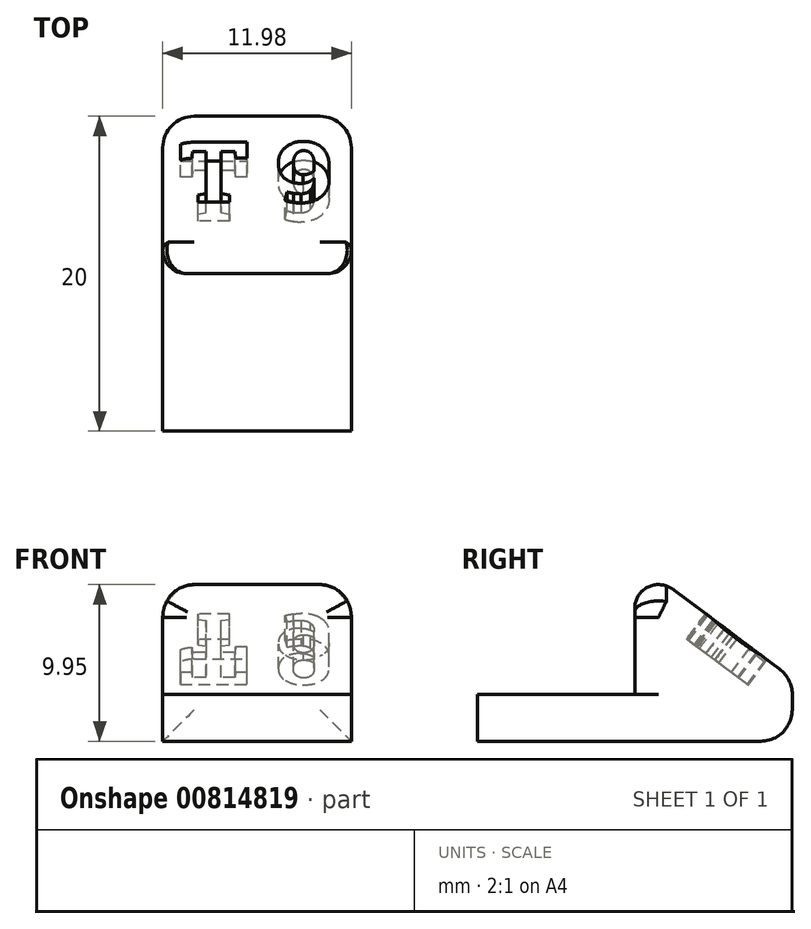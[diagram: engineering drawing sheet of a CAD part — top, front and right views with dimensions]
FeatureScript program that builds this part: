
annotation { "Feature Type Name" : "Feature", "Feature Type Description" : "" }
export const myFeature = defineFeature(function(context is Context, id is Id, definition is map)
    precondition{}
    {
        {
            var Q0;
            Q0=qCreatedBy(makeId("Top.planeOp"),FACE);
            var sketch = newSketch(context, id + "F0", { "sketchPlane" : qUnion([Q0])});
            skLineSegment(sketch, "E0.bottom", {"start": v(6, 10) * mm, "end": v(-5.99, 10) * mm});
            skLineSegment(sketch, "E0.top", {"start": v(6, -10) * mm, "end": v(-5.99, -10) * mm});
            skLineSegment(sketch, "E0.left", {"start": v(6, 10) * mm, "end": v(6, -10) * mm});
            skLineSegment(sketch, "E0.right", {"start": v(-5.99, 10) * mm, "end": v(-5.99, -10) * mm});
            skPoint(sketch, "E0.middle", {"position": v(0, 0) * mm});
            skSolve(sketch);
        }
        {
            var Q0;
            Q0=qSketchRegion(id+"F0",true);
            extrude(context, id + "F1", {"entities" : qUnion([Q0]), "depth" : 2.98 * mm, "offsetDistance" : 25 * mm});
        }
        {
            var Q0;
            Q0=makeQuery(id+"F1.opExtrude","CAP_FACE",FACE,{"disambiguationData":[OSD([sQuery(id+"F0.wireOp",EDGE,"E0.bottom"),sQuery(id+"F0.wireOp",EDGE,"E0.top"),sQuery(id+"F0.wireOp",EDGE,"E0.left"),sQuery(id+"F0.wireOp",EDGE,"E0.right")])],"isStart":false});
            var sketch = newSketch(context, id + "F2", { "sketchPlane" : qUnion([Q0])});
            skLineSegment(sketch, "E1.bottom", {"start": v(-5.99, 10) * mm, "end": v(6, 10) * mm});
            skLineSegment(sketch, "E1.top", {"start": v(-5.99, 0) * mm, "end": v(6, 0) * mm});
            skLineSegment(sketch, "E1.left", {"start": v(-5.99, 10) * mm, "end": v(-5.99, 0) * mm});
            skLineSegment(sketch, "E1.right", {"start": v(6, 10) * mm, "end": v(6, 0) * mm});
            skSolve(sketch);
        }
        {
            var Q0;
            Q0=makeQuery(id+"F2.imprint","IMPRINT",FACE,{"disambiguationData":[TD([[makeQuery(id+"F2.imprint","IMPRINT",EDGE,{"derivedFrom":sQuery(id+"F2.wireOp",EDGE,"E1.bottom")}),1.0]])]});
            extrude(context, id + "F3", {"entities" : qUnion([Q0]), "operationType" : NewBodyOperationType.ADD, "depth" : 7 * mm, "offsetDistance" : 25 * mm});
        }
        {
            var Q0;
            Q0=makeQuery(id+"F3.opExtrude","CAP_EDGE",EDGE,{"disambiguationData":[OSD([sQuery(id+"F2.wireOp",EDGE,"E1.bottom")])],"isStart":false});
            chamfer(context, id + "F4", {"entities" : qUnion([Q0]), "chamferType" : ChamferType.TWO_OFFSETS, "width1" : 8 * mm, "oppositeDirection" : false, "width2" : 6 * mm, "tangentPropagation" : true});
        }
        {
            var Q0;
            Q0=makeQuery(id+"F4.opChamfer","BLEND_FACE",FACE,{"disambiguationData":[OSD([sQuery(id+"F2.wireOp",EDGE,"E1.bottom")])]});
            var sketch = newSketch(context, id + "F5", { "sketchPlane" : qUnion([Q0])});
            skText(sketch, "E2", { "text": "T 9", "fontName": "RobotoSlab-Bold.ttf"});
            skPoint(sketch, "E3", {"position": v(-4.05, -0.08) * mm});
            const initialGuessF5  = {"E2": [-0.005, -0.00121, 1, 0, 0.00482]};
            skSetInitialGuess(sketch, initialGuessF5);
            skSolve(sketch);
        }
        {
            var Q0;
            Q0 = qSketchRegion(id + "F5", true);
            extrude(context, id + "F6", {"entities" : qUnion([Q0]), "operationType" : NewBodyOperationType.REMOVE, "oppositeDirection" : true, "depth" : 2 * mm, "offsetDistance" : 25 * mm});
        }
        {
            var Q0;
            {var subQ0=sQuery(id+"F2.wireOp",EDGE,"E1.bottom");Q0=makeQuery(id+"F4.opChamfer","BLEND_EDGE",EDGE,{"blendedFrom":[makeQuery(id+"F3.opExtrude","CAP_EDGE",EDGE,{"disambiguationData":[OSD([subQ0])],"isStart":false}),makeQuery(id+"F3.boolean.opBoolean","MERGE",FACE,{"derivedFrom":[makeQuery(id+"F1.opExtrude","SWEPT_FACE",FACE,{"disambiguationData":[OSD([sQuery(id+"F0.wireOp",EDGE,"E0.bottom")])]}),makeQuery(id+"F3.opExtrude","SWEPT_FACE",FACE,{"disambiguationData":[OSD([subQ0])]})]})],"blendedInto":[makeQuery(id+"F3.boolean.opBoolean","MERGE",FACE,{"derivedFrom":[makeQuery(id+"F1.opExtrude","SWEPT_FACE",FACE,{"disambiguationData":[OSD([sQuery(id+"F0.wireOp",EDGE,"E0.bottom")])]}),makeQuery(id+"F3.opExtrude","SWEPT_FACE",FACE,{"disambiguationData":[OSD([subQ0])]})]})]});}
            var Q1;
            Q1=makeQuery(id+"F1.opExtrude","CAP_EDGE",EDGE,{"disambiguationData":[OSD([sQuery(id+"F0.wireOp",EDGE,"E0.bottom")])],"isStart":true});
            var Q2;
            Q2=makeQuery(id+"F3.boolean.opBoolean","MERGE",EDGE,{"derivedFrom":[makeQuery(id+"F1.opExtrude","SWEPT_EDGE",EDGE,{"disambiguationData":[OSD([sQuery(id+"F0.wireOp",EDGE,"E0.bottom"),sQuery(id+"F0.wireOp",EDGE,"E0.right")])]}),makeQuery(id+"F3.opExtrude","SWEPT_EDGE",EDGE,{"disambiguationData":[OSD([sQuery(id+"F2.wireOp",EDGE,"E1.bottom"),sQuery(id+"F2.wireOp",EDGE,"E1.left")])]})]});
            var Q3;
            Q3=makeQuery(id+"F3.boolean.opBoolean","MERGE",EDGE,{"derivedFrom":[makeQuery(id+"F1.opExtrude","SWEPT_EDGE",EDGE,{"disambiguationData":[OSD([sQuery(id+"F0.wireOp",EDGE,"E0.bottom"),sQuery(id+"F0.wireOp",EDGE,"E0.left")])]}),makeQuery(id+"F3.opExtrude","SWEPT_EDGE",EDGE,{"disambiguationData":[OSD([sQuery(id+"F2.wireOp",EDGE,"E1.bottom"),sQuery(id+"F2.wireOp",EDGE,"E1.right")])]})]});
            var Q4;
            Q4=makeQuery(id+"F4.opChamfer","BLEND_EDGE",EDGE,{"blendedFrom":[makeQuery(id+"F3.opExtrude","CAP_EDGE",EDGE,{"disambiguationData":[OSD([sQuery(id+"F2.wireOp",EDGE,"E1.bottom")])],"isStart":false}),makeQuery(id+"F3.boolean.opBoolean","MERGE",FACE,{"derivedFrom":[makeQuery(id+"F1.opExtrude","SWEPT_FACE",FACE,{"disambiguationData":[OSD([sQuery(id+"F0.wireOp",EDGE,"E0.left")])]}),makeQuery(id+"F3.opExtrude","SWEPT_FACE",FACE,{"disambiguationData":[OSD([sQuery(id+"F2.wireOp",EDGE,"E1.right")])]})]})],"blendedInto":[makeQuery(id+"F3.boolean.opBoolean","MERGE",FACE,{"derivedFrom":[makeQuery(id+"F1.opExtrude","SWEPT_FACE",FACE,{"disambiguationData":[OSD([sQuery(id+"F0.wireOp",EDGE,"E0.left")])]}),makeQuery(id+"F3.opExtrude","SWEPT_FACE",FACE,{"disambiguationData":[OSD([sQuery(id+"F2.wireOp",EDGE,"E1.right")])]})]})]});
            var Q5;
            Q5=makeQuery(id+"F4.opChamfer","BLEND_EDGE",EDGE,{"blendedFrom":[makeQuery(id+"F3.opExtrude","CAP_EDGE",EDGE,{"disambiguationData":[OSD([sQuery(id+"F2.wireOp",EDGE,"E1.bottom")])],"isStart":false}),makeQuery(id+"F3.boolean.opBoolean","MERGE",FACE,{"derivedFrom":[makeQuery(id+"F1.opExtrude","SWEPT_FACE",FACE,{"disambiguationData":[OSD([sQuery(id+"F0.wireOp",EDGE,"E0.right")])]}),makeQuery(id+"F3.opExtrude","SWEPT_FACE",FACE,{"disambiguationData":[OSD([sQuery(id+"F2.wireOp",EDGE,"E1.left")])]})]})],"blendedInto":[makeQuery(id+"F3.boolean.opBoolean","MERGE",FACE,{"derivedFrom":[makeQuery(id+"F1.opExtrude","SWEPT_FACE",FACE,{"disambiguationData":[OSD([sQuery(id+"F0.wireOp",EDGE,"E0.right")])]}),makeQuery(id+"F3.opExtrude","SWEPT_FACE",FACE,{"disambiguationData":[OSD([sQuery(id+"F2.wireOp",EDGE,"E1.left")])]})]})]});
            var Q6;
            Q6=makeQuery(id+"F3.opExtrude","CAP_EDGE",EDGE,{"disambiguationData":[OSD([sQuery(id+"F2.wireOp",EDGE,"E1.right")])],"isStart":false});
            var Q7;
            Q7=makeQuery(id+"F3.opExtrude","CAP_EDGE",EDGE,{"disambiguationData":[OSD([sQuery(id+"F2.wireOp",EDGE,"E1.left")])],"isStart":false});
            var Q8;
            {var subQ0=sQuery(id+"F2.wireOp",EDGE,"E1.bottom");Q8=makeQuery(id+"F4.opChamfer","BLEND_EDGE",EDGE,{"blendedFrom":[makeQuery(id+"F3.opExtrude","CAP_EDGE",EDGE,{"disambiguationData":[OSD([subQ0])],"isStart":false}),makeQuery(id+"F3.opExtrude","CAP_FACE",FACE,{"disambiguationData":[OSD([subQ0,sQuery(id+"F2.wireOp",EDGE,"E1.top"),sQuery(id+"F2.wireOp",EDGE,"E1.left"),sQuery(id+"F2.wireOp",EDGE,"E1.right")])],"isStart":false})],"blendedInto":[makeQuery(id+"F3.opExtrude","CAP_FACE",FACE,{"disambiguationData":[OSD([subQ0,sQuery(id+"F2.wireOp",EDGE,"E1.top"),sQuery(id+"F2.wireOp",EDGE,"E1.left"),sQuery(id+"F2.wireOp",EDGE,"E1.right")])],"isStart":false})]});}
            fillet(context, id + "F7", {"entities" : qUnion([Q0, Q1, Q2, Q3, Q4, Q5, Q6, Q7, Q8]), "radius" : 2 * mm, "tangentPropagation" : true, "allowEdgeOverflow" : false});
        }
        {
            var Q0;
            Q0=makeQuery(id+"F3.opExtrude","CAP_EDGE",EDGE,{"disambiguationData":[OSD([sQuery(id+"F2.wireOp",EDGE,"E1.top")])],"isStart":false});
            fillet(context, id + "F8", {"entities" : qUnion([Q0]), "radius" : 1.5 * mm, "tangentPropagation" : true, "allowEdgeOverflow" : false});
        }
    });
